# Revit family: Plaster Accessories-Ventilated Screed-Section
name_source: partatom
category: Detail Items
revit_build: Autodesk Revit Architecture 2012 (Build: 20110210_1515)
units: mm (PartAtom-declared; Revit-internal decimal feet)

## types (12) — shared parameters

## per-type parameters (varying)
| type | Depth | Keynote | Width |
| 3/4" x 1" | 0' - 0 3/4" | 09 22 36.G1 | 0' - 1" |
| 3/4" x 1 1/2" | 0' - 0 3/4" | 09 22 36.G2 | 0' - 1 1/2" |
| 3/4" x 2" | 0' - 0 3/4" | 09 22 36.G3 | 0' - 2" |
| 3/4" x 2 1/2" | 0' - 0 3/4" | 09 22 36.G4 | 0' - 2 1/2" |
| 3/4" x 4" | 0' - 0 3/4" | 09 22 36.G6 | 0' - 4" |
| 3/4" x 3 1/2" | 0' - 0 3/4" | 09 22 36.G5 | 0' - 3 1/2" |
| 7/8" x 1" | 0' - 0 7/8" | 09 22 36.G7 | 0' - 1" |
| 7/8" x 1 1/2" | 0' - 0 7/8" | 09 22 36.G8 | 0' - 1 1/2" |
| 7/8" x 2" | 0' - 0 7/8" | 09 22 36.G9 | 0' - 2" |
| 7/8" x 2 1/2" | 0' - 0 7/8" | 09 22 36.G10 | 0' - 2 1/2" |
| 7/8" x 3 1/2" | 0' - 0 7/8" | 09 22 36.G11 | 0' - 3 1/2" |
| 7/8" x 4" | 0' - 0 7/8" | 09 22 36.G12 | 0' - 4" |

## geometry (parser evidence)
native form markers: Sweep x1
no freeform markers — native parametric forms only
